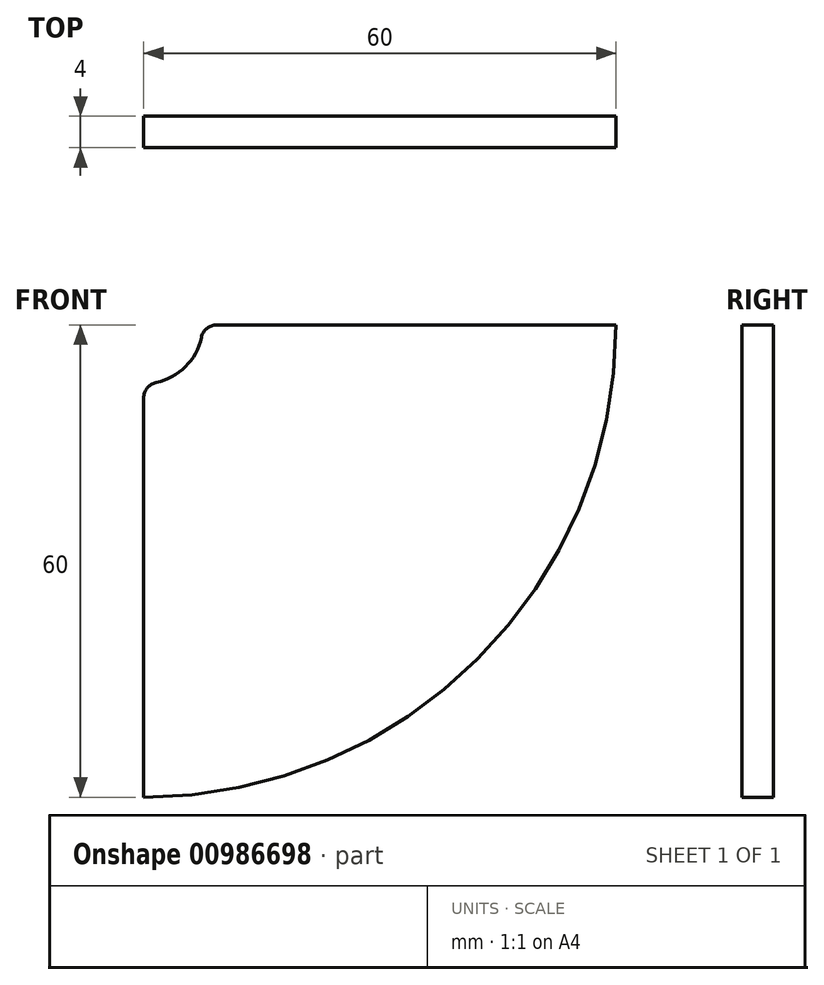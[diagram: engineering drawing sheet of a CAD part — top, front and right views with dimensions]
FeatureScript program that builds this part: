
annotation { "Feature Type Name" : "Feature", "Feature Type Description" : "" }
export const myFeature = defineFeature(function(context is Context, id is Id, definition is map)
    precondition{}
    {
        {
            var Q0;
            Q0=qCreatedBy(makeId("Front.planeOp"),FACE);
            var sketch = newSketch(context, id + "F0", { "sketchPlane" : qUnion([Q0])});
            skLineSegment(sketch, "E0", {"start": v(9.29, 0) * mm, "end": v(60, 0) * mm});
            skArc(sketch, "E1", {"start": v(60, 0) * mm, "mid": v(42.43, -42.43) * mm, "end": v(0, -60) * mm});
            skLineSegment(sketch, "E2", {"start": v(0, -9.29) * mm, "end": v(0, -60) * mm});
            skArc(sketch, "E3", {"start": v(1.58, -7.33) * mm, "mid": v(5.3, -5.3) * mm, "end": v(7.33, -1.58) * mm});
            skPoint(sketch, "E4.visualSharp", {"position": v(7.5, 0) * mm});
            skArc(sketch, "E4.filletArc", {"start": v(9.29, 0) * mm, "mid": v(8.03, -0.44) * mm, "end": v(7.33, -1.58) * mm});
            skPoint(sketch, "E5.visualSharp", {"position": v(0, -7.5) * mm});
            skArc(sketch, "E5.filletArc", {"start": v(1.58, -7.33) * mm, "mid": v(0.44, -8.03) * mm, "end": v(0, -9.29) * mm});
            skSolve(sketch);
        }
        {
            var Q0;
            Q0=makeQuery(id+"F0.imprint","IMPRINT",FACE,{"disambiguationData":[TD([[makeQuery(id+"F0.imprint","IMPRINT",EDGE,{"derivedFrom":sQuery(id+"F0.wireOp",EDGE,"E0")}),-1.0]])]});
            extrude(context, id + "F1", {"entities" : qUnion([Q0]), "depth" : 4 * mm, "offsetDistance" : 25 * mm});
        }
    });
